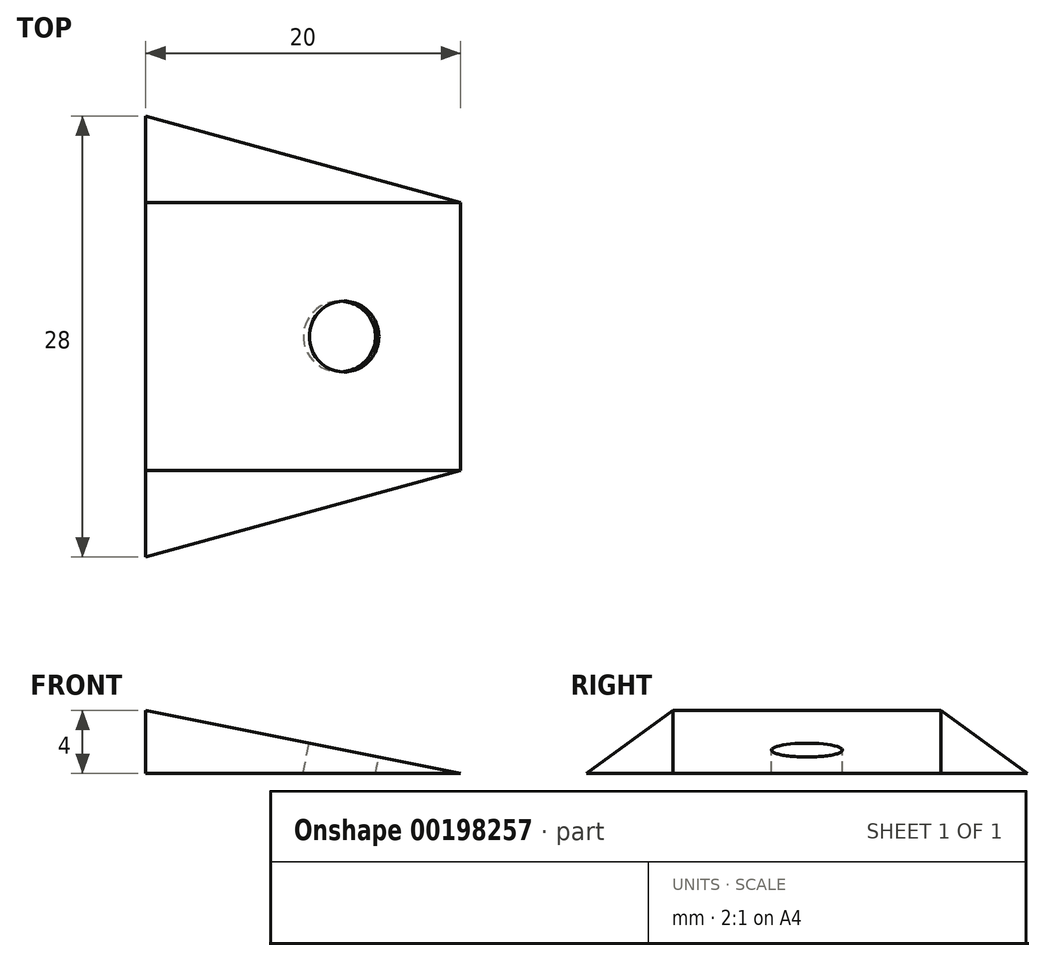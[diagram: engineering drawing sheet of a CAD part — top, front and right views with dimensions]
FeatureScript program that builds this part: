
annotation { "Feature Type Name" : "Feature", "Feature Type Description" : "" }
export const myFeature = defineFeature(function(context is Context, id is Id, definition is map)
    precondition{}
    {
        {
            var Q0;
            Q0=qCreatedBy(makeId("Top.planeOp"),FACE);
            var sketch = newSketch(context, id + "F0", { "sketchPlane" : qUnion([Q0])});
            skLineSegment(sketch, "E0", {"start": v(0, 8.5) * mm, "end": v(0, -8.5) * mm});
            skLineSegment(sketch, "E1", {"start": v(0, -8.5) * mm, "end": v(-20, -14) * mm});
            skLineSegment(sketch, "E2", {"start": v(-20, -14) * mm, "end": v(-20, 14) * mm});
            skLineSegment(sketch, "E3", {"start": v(-20, 14) * mm, "end": v(0, 8.5) * mm});
            skLineSegment(sketch, "E4.bottom", {"start": v(-20, -14) * mm, "end": v(0, -14) * mm});
            skLineSegment(sketch, "E4.top", {"start": v(-20, 14) * mm, "end": v(0, 14) * mm});
            skLineSegment(sketch, "E4.right", {"start": v(0, -14) * mm, "end": v(0, 14) * mm});
            skSolve(sketch);
        }
        {
            var Q0;
            Q0=sQuery(id+"F0.wireOp",EDGE,"E2");
            cPlane(context, id + "F1", {"entities" : qUnion([Q0]), "cplaneType" : CPlaneType.LINE_ANGLE, "offset" : 25 * mm, "angle" : 90 * degree, "width" : 150 * mm, "height" : 150 * mm});
        }
        {
            var Q0;
            Q0=qCreatedBy(id+"F1.planeOp",FACE);
            var sketch = newSketch(context, id + "F2", { "sketchPlane" : qUnion([Q0])});
            skLineSegment(sketch, "E5", {"start": v(14, 0) * mm, "end": v(8.5, 4) * mm});
            skLineSegment(sketch, "E6", {"start": v(8.5, 4) * mm, "end": v(-8.5, 4) * mm});
            skLineSegment(sketch, "E7", {"start": v(-8.5, 4) * mm, "end": v(-14, 0) * mm});
            skLineSegment(sketch, "E8", {"start": v(-14, 0) * mm, "end": v(14, 0) * mm});
            skSolve(sketch);
        }
        {
            var Q0;
            Q0=makeQuery(id+"F2.imprint","IMPRINT",FACE,{"disambiguationData":[TD([[makeQuery(id+"F2.imprint","IMPRINT",EDGE,{"derivedFrom":sQuery(id+"F2.wireOp",EDGE,"E5")}),1.0]])]});
            extrude(context, id + "F3", {"entities" : qUnion([Q0]), "depth" : 20 * mm});
        }
        {
            var Q0;
            {var subQ0=sQuery(id+"F0.wireOp",EDGE,"E1");Q0=makeQuery(id+"F0.imprint","IMPRINT",FACE,{"disambiguationData":[TD([[makeQuery(id+"F0.imprint","IMPRINT",EDGE,{"derivedFrom":subQ0}),1.0]])]});}
            var Q1;
            {var subQ0=sQuery(id+"F0.wireOp",EDGE,"E3");Q1=makeQuery(id+"F0.imprint","IMPRINT",FACE,{"disambiguationData":[TD([[makeQuery(id+"F0.imprint","IMPRINT",EDGE,{"derivedFrom":subQ0}),1.0]])]});}
            extrude(context, id + "F4", {"entities" : qUnion([Q0, Q1]), "operationType" : NewBodyOperationType.REMOVE, "depth" : 25 * mm});
        }
        {
            var Q0;
            Q0=qCreatedBy(makeId("Front.planeOp"),FACE);
            var sketch = newSketch(context, id + "F5", { "sketchPlane" : qUnion([Q0])});
            skLineSegment(sketch, "E9", {"start": v(0, 0) * mm, "end": v(0, 4) * mm});
            skLineSegment(sketch, "E10", {"start": v(0, 4) * mm, "end": v(-20, 4) * mm});
            skLineSegment(sketch, "E11", {"start": v(-20, 4) * mm, "end": v(0, 0) * mm});
            skSolve(sketch);
        }
        {
            var Q0;
            Q0 = qSketchRegion(id + "F5", true);
            extrude(context, id + "F6", {"entities" : qUnion([Q0]), "operationType" : NewBodyOperationType.REMOVE, "endBound" : BoundingType.SYMMETRIC, "oppositeDirection" : true, "depth" : 25 * mm});
        }
        {
            var Q0;
            Q0=makeQuery(id+"F3.opExtrude","CAP_VERTEX",VERTEX,{"disambiguationData":[OSD([sQuery(id+"F2.wireOp",EDGE,"E5"),sQuery(id+"F2.wireOp",EDGE,"E6")])],"isStart":true});
            var Q1;
            Q1=makeQuery(id+"F4.boolean.opBoolean","MERGE",VERTEX,{"derivedFrom":[makeQuery(id+"F3.opExtrude","CAP_VERTEX",VERTEX,{"disambiguationData":[OSD([sQuery(id+"F2.wireOp",EDGE,"E5"),sQuery(id+"F2.wireOp",EDGE,"E8")])],"isStart":true}),makeQuery(id+"F4.opExtrude","CAP_VERTEX",VERTEX,{"disambiguationData":[OSD([sQuery(id+"F0.wireOp",EDGE,"E3"),sQuery(id+"F0.wireOp",EDGE,"E4.top"),sQuery(id+"F0.wireOp",EDGE,"E2")])],"isStart":true})]});
            var Q2;
            Q2=makeQuery(id+"F4.boolean.opBoolean","COPY",VERTEX,{"derivedFrom":makeQuery(id+"F4.opExtrude","CAP_VERTEX",VERTEX,{"disambiguationData":[OSD([sQuery(id+"F0.wireOp",EDGE,"E3"),sQuery(id+"F0.wireOp",EDGE,"E4.right")])],"isStart":true})});
            cPlane(context, id + "F7", {"entities" : qUnion([Q0, Q1, Q2]), "cplaneType" : CPlaneType.THREE_POINT, "offset" : 25 * mm, "width" : 150 * mm, "height" : 150 * mm});
        }
        {
            var Q0;
            Q0=qCreatedBy(id+"F7.planeOp",FACE);
            var sketch = newSketch(context, id + "F8", { "sketchPlane" : qUnion([Q0])});
            skLineSegment(sketch, "E12.bottom", {"start": v(2.72, 0.9) * mm, "end": v(-27.47, 0.9) * mm});
            skLineSegment(sketch, "E12.top", {"start": v(2.72, 14.25) * mm, "end": v(-27.47, 14.25) * mm});
            skLineSegment(sketch, "E12.left", {"start": v(2.72, 0.9) * mm, "end": v(2.72, 14.25) * mm});
            skLineSegment(sketch, "E12.right", {"start": v(-27.47, 0.9) * mm, "end": v(-27.47, 14.25) * mm});
            skSolve(sketch);
        }
        {
            var Q0;
            Q0=makeQuery(id+"F8.imprint","IMPRINT",FACE,{"disambiguationData":[TD([[makeQuery(id+"F8.imprint","IMPRINT",EDGE,{"derivedFrom":sQuery(id+"F8.wireOp",EDGE,"E12.bottom")}),-1.0]])]});
            extrude(context, id + "F9", {"entities" : qUnion([Q0]), "operationType" : NewBodyOperationType.REMOVE, "depth" : 25 * mm});
        }
        {
            var Q0;
            Q0=makeQuery(id+"F4.boolean.opBoolean","MERGE",VERTEX,{"derivedFrom":[makeQuery(id+"F3.opExtrude","CAP_VERTEX",VERTEX,{"disambiguationData":[OSD([sQuery(id+"F2.wireOp",EDGE,"E7"),sQuery(id+"F2.wireOp",EDGE,"E8")])],"isStart":true}),makeQuery(id+"F4.opExtrude","CAP_VERTEX",VERTEX,{"disambiguationData":[OSD([sQuery(id+"F0.wireOp",EDGE,"E1"),sQuery(id+"F0.wireOp",EDGE,"E4.bottom"),sQuery(id+"F0.wireOp",EDGE,"E2")])],"isStart":true})]});
            var Q1;
            Q1=makeQuery(id+"F3.opExtrude","CAP_VERTEX",VERTEX,{"disambiguationData":[OSD([sQuery(id+"F2.wireOp",EDGE,"E6"),sQuery(id+"F2.wireOp",EDGE,"E7")])],"isStart":true});
            var Q2;
            Q2=makeQuery(id+"F4.boolean.opBoolean","COPY",VERTEX,{"derivedFrom":makeQuery(id+"F4.opExtrude","CAP_VERTEX",VERTEX,{"disambiguationData":[OSD([sQuery(id+"F0.wireOp",EDGE,"E1"),sQuery(id+"F0.wireOp",EDGE,"E4.right")])],"isStart":true})});
            cPlane(context, id + "F10", {"entities" : qUnion([Q0, Q1, Q2]), "cplaneType" : CPlaneType.THREE_POINT, "offset" : 25 * mm, "width" : 150 * mm, "height" : 150 * mm});
        }
        {
            var Q0;
            Q0=qCreatedBy(id+"F10.planeOp",FACE);
            var sketch = newSketch(context, id + "F11", { "sketchPlane" : qUnion([Q0])});
            skLineSegment(sketch, "E13.bottom", {"start": v(-24.12, -14.9) * mm, "end": v(0, -14.9) * mm});
            skLineSegment(sketch, "E13.top", {"start": v(-24.12, 2.46) * mm, "end": v(0, 2.46) * mm});
            skLineSegment(sketch, "E13.left", {"start": v(-24.12, -14.9) * mm, "end": v(-24.12, 2.46) * mm});
            skLineSegment(sketch, "E13.right", {"start": v(0, -14.9) * mm, "end": v(0, 2.46) * mm});
            skSolve(sketch);
        }
        {
            var Q0;
            Q0=makeQuery(id+"F11.imprint","IMPRINT",FACE,{"disambiguationData":[TD([[makeQuery(id+"F11.imprint","IMPRINT",EDGE,{"derivedFrom":sQuery(id+"F11.wireOp",EDGE,"E13.bottom")}),1.0]])]});
            extrude(context, id + "F12", {"entities" : qUnion([Q0]), "operationType" : NewBodyOperationType.REMOVE, "depth" : 25 * mm});
        }
        {
            var Q0;
            Q0=makeQuery(id+"F6.boolean.opBoolean","COPY",FACE,{"derivedFrom":makeQuery(id+"F6.opExtrude","SWEPT_FACE",FACE,{"disambiguationData":[OSD([sQuery(id+"F5.wireOp",EDGE,"E11")])]})});
            var sketch = newSketch(context, id + "F13", { "sketchPlane" : qUnion([Q0])});
            skCircle(sketch, "E14", {"center": v(-7.55, 0) * mm, "radius": 2.25 * mm});
            skSolve(sketch);
        }
        {
            var Q0;
            Q0=makeQuery(id+"F13.imprint","IMPRINT",FACE,{"disambiguationData":[TD([[makeQuery(id+"F13.imprint","IMPRINT",EDGE,{"derivedFrom":sQuery(id+"F13.wireOp",EDGE,"E14")}),1.0]])]});
            extrude(context, id + "F14", {"entities" : qUnion([Q0]), "operationType" : NewBodyOperationType.REMOVE, "oppositeDirection" : true, "depth" : 25 * mm});
        }
    });
